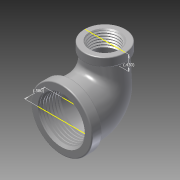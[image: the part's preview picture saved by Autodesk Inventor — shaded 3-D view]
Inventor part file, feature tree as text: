
AUTODESK INVENTOR PART (.ipt)
format: ipt  version: 2014 (Build 180170000, 170)  size: 1,787,904 bytes
history: native  units: in
note: dims shown in document units (in); Inventor stores cm internally (conversion verified against a paired STEP export)
features: other x2, sketch x2, imported_body x1
ambient origin geometry x8: Origin, YZ Plane, XZ Plane, XY Plane, X Axis, Y Axis, Z Axis, Center Point
bodies: Body1 (feature_tree)
feature tree (5):
  parser-record x1  (decoder bookkeeping rows leaked as tree rows — omitted from the tree; the rows remain in map.json)
  other  "44605K4221"
  sketch  "Sketch1"  dims[d0=0.43in]
  sketch  "Sketch2"  dims[d1=0.58in]
  imported_body  "Base1"
